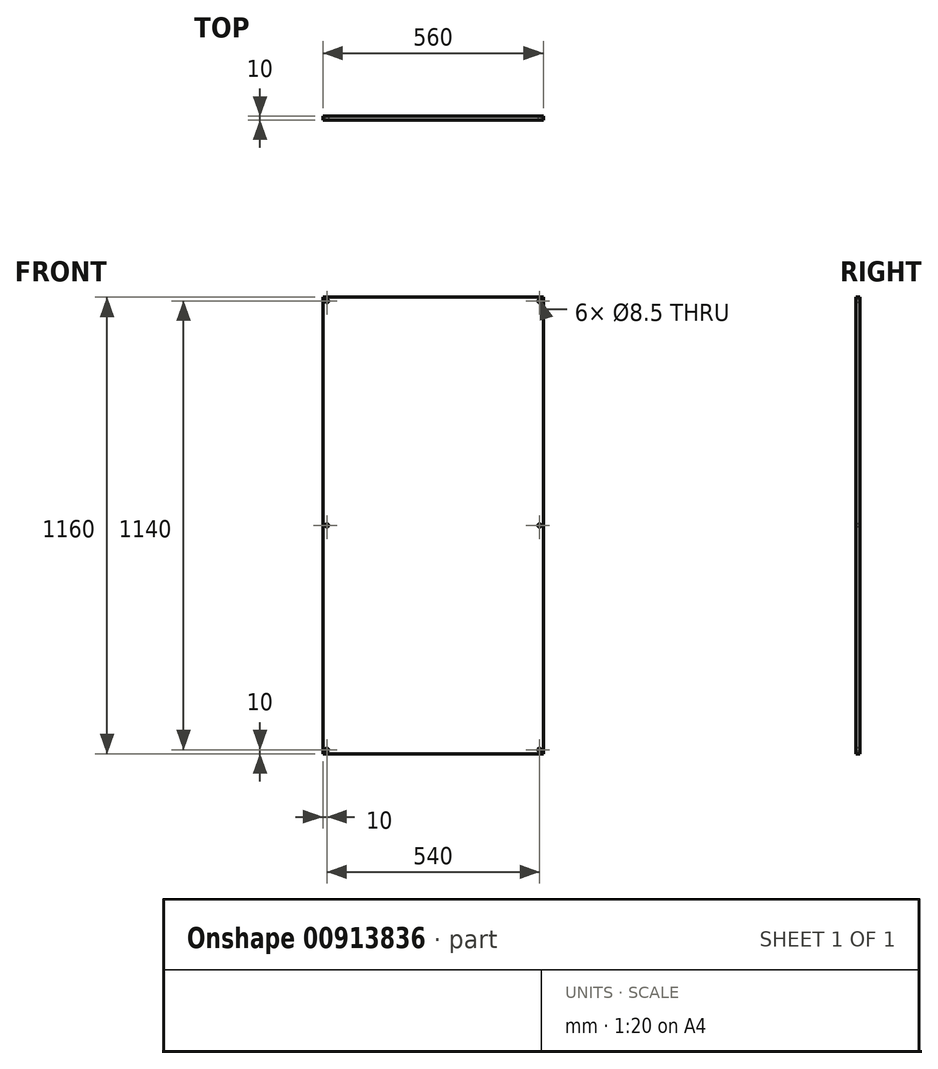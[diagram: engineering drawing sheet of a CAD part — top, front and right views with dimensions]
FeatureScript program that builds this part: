
annotation { "Feature Type Name" : "Feature", "Feature Type Description" : "" }
export const myFeature = defineFeature(function(context is Context, id is Id, definition is map)
    precondition{}
    {
        {
            var Q0;
            Q0=qCreatedBy(makeId("Front.planeOp"),FACE);
            var sketch = newSketch(context, id + "F0", { "sketchPlane" : qUnion([Q0])});
            skLineSegment(sketch, "E0.bottom", {"start": v(280, 580) * mm, "end": v(-280, 580) * mm});
            skLineSegment(sketch, "E0.top", {"start": v(280, -580) * mm, "end": v(-280, -580) * mm});
            skLineSegment(sketch, "E0.left", {"start": v(280, 580) * mm, "end": v(280, -580) * mm});
            skLineSegment(sketch, "E0.right", {"start": v(-280, 580) * mm, "end": v(-280, -580) * mm});
            skPoint(sketch, "E0.middle", {"position": v(0, 0) * mm});
            skSolve(sketch);
        }
        {
            var Q0;
            Q0=makeQuery(id+"F0.imprint","IMPRINT",FACE,{"disambiguationData":[TD([[makeQuery(id+"F0.imprint","IMPRINT",EDGE,{"derivedFrom":sQuery(id+"F0.wireOp",EDGE,"E0.bottom")}),1.0]])]});
            extrude(context, id + "F1", {"entities" : qUnion([Q0]), "depth" : 10 * mm, "offsetDistance" : 25 * mm});
        }
        {
            var Q0;
            Q0=makeQuery(id+"F1.opExtrude","CAP_FACE",FACE,{"disambiguationData":[OSD([sQuery(id+"F0.wireOp",EDGE,"E0.bottom"),sQuery(id+"F0.wireOp",EDGE,"E0.top"),sQuery(id+"F0.wireOp",EDGE,"E0.left"),sQuery(id+"F0.wireOp",EDGE,"E0.right")])],"isStart":false});
            var sketch = newSketch(context, id + "F2", { "sketchPlane" : qUnion([Q0])});
            skLineSegment(sketch, "E1.0", {"start": v(-270, -570) * mm, "end": v(270, -570) * mm});
            skLineSegment(sketch, "E1.1", {"start": v(-270, 570) * mm, "end": v(-270, -570) * mm});
            skLineSegment(sketch, "E1.2", {"start": v(270, 570) * mm, "end": v(-270, 570) * mm});
            skLineSegment(sketch, "E1.3", {"start": v(270, -570) * mm, "end": v(270, 570) * mm});
            skPoint(sketch, "E2", {"position": v(-270, -570) * mm});
            skPoint(sketch, "E3", {"position": v(270, -570) * mm});
            skPoint(sketch, "E4", {"position": v(270, 0) * mm});
            skPoint(sketch, "E5", {"position": v(-270, 0) * mm});
            skPoint(sketch, "E6", {"position": v(-270, 570) * mm});
            skPoint(sketch, "E7", {"position": v(270, 570) * mm});
            skSolve(sketch);
        }
        {
            var Q0;
            Q0=sQuery(id+"F2.wireOp",VERTEX,"E6");
            var Q1;
            Q1=sQuery(id+"F2.wireOp",VERTEX,"E7");
            var Q2;
            Q2=sQuery(id+"F2.wireOp",VERTEX,"E4");
            var Q3;
            Q3=sQuery(id+"F2.wireOp",VERTEX,"E5");
            var Q4;
            Q4=sQuery(id+"F2.wireOp",VERTEX,"E2");
            var Q5;
            Q5=sQuery(id+"F2.wireOp",VERTEX,"E3");
            var Q6;
            Q6=makeQuery(id+"F1.opExtrude","SWEPT_BODY",BODY,{"disambiguationData":[OSD([sQuery(id+"F0.wireOp",EDGE,"E0.bottom"),sQuery(id+"F0.wireOp",EDGE,"E0.top"),sQuery(id+"F0.wireOp",EDGE,"E0.left"),sQuery(id+"F0.wireOp",EDGE,"E0.right")])]});
            hole(context, id + "F3", {"style" : HoleStyle.SIMPLE, "endStyle" : HoleEndStyle.THROUGH, "holeDiameter" : 8.5 * mm, "majorDiameter" : 5 * mm, "isTappedThrough" : true, "tappedDepth" : 12 * mm, "tapClearance" : 3, "locations" : qUnion([Q0, Q1, Q2, Q3, Q4, Q5]), "scope" : qUnion([Q6])});
        }
    });
